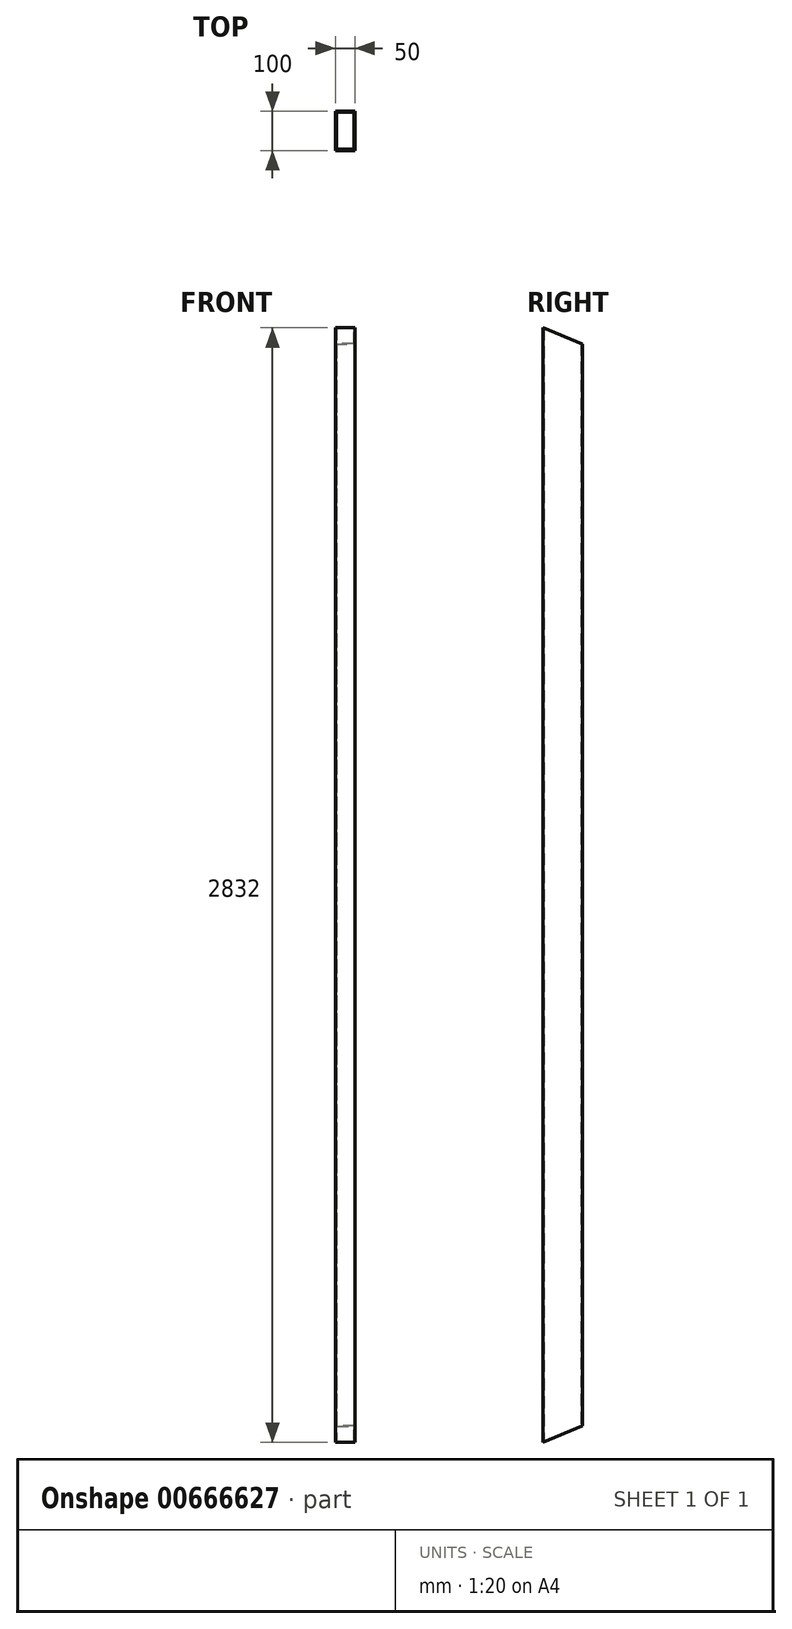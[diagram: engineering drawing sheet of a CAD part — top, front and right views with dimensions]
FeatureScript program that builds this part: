
annotation { "Feature Type Name" : "Feature", "Feature Type Description" : "" }
export const myFeature = defineFeature(function(context is Context, id is Id, definition is map)
    precondition{}
    {
        {
            var Q0;
            Q0=qCreatedBy(makeId("Top.planeOp"),FACE);
            var sketch = newSketch(context, id + "F0", { "sketchPlane" : qUnion([Q0])});
            skLineSegment(sketch, "E0.bottom", {"start": v(25, 50) * mm, "end": v(-25, 50) * mm});
            skLineSegment(sketch, "E0.top", {"start": v(25, -50) * mm, "end": v(-25, -50) * mm});
            skLineSegment(sketch, "E0.left", {"start": v(25, 50) * mm, "end": v(25, -50) * mm});
            skLineSegment(sketch, "E0.right", {"start": v(-25, 50) * mm, "end": v(-25, -50) * mm});
            skPoint(sketch, "E0.middle", {"position": v(0, 0) * mm});
            skLineSegment(sketch, "E1.bottom", {"start": v(22, 47) * mm, "end": v(-22, 47) * mm});
            skLineSegment(sketch, "E1.top", {"start": v(22, -47) * mm, "end": v(-22, -47) * mm});
            skLineSegment(sketch, "E1.left", {"start": v(22, 47) * mm, "end": v(22, -47) * mm});
            skLineSegment(sketch, "E1.right", {"start": v(-22, 47) * mm, "end": v(-22, -47) * mm});
            skSolve(sketch);
        }
        {
            var Q0;
            Q0=makeQuery(id+"F0.imprint","IMPRINT",FACE,{"disambiguationData":[TD([[makeQuery(id+"F0.imprint","IMPRINT",EDGE,{"derivedFrom":sQuery(id+"F0.wireOp",EDGE,"E0.bottom")}),1.0]])]});
            extrude(context, id + "F1", {"entities" : qUnion([Q0]), "depth" : 2832 * mm, "offsetDistance" : 25 * mm});
        }
        {
            var Q0;
            Q0=makeQuery(id+"F1.opExtrude","CAP_EDGE",EDGE,{"disambiguationData":[OSD([sQuery(id+"F0.wireOp",EDGE,"E0.bottom")])],"isStart":false});
            chamfer(context, id + "F2", {"entities" : qUnion([Q0]), "chamferType" : ChamferType.TWO_OFFSETS, "width1" : 100 * mm, "oppositeDirection" : false, "width2" : 42 * mm, "tangentPropagation" : true});
        }
        {
            var Q0;
            Q0=makeQuery(id+"F1.opExtrude","CAP_EDGE",EDGE,{"disambiguationData":[OSD([sQuery(id+"F0.wireOp",EDGE,"E0.bottom")])],"isStart":true});
            chamfer(context, id + "F3", {"entities" : qUnion([Q0]), "chamferType" : ChamferType.TWO_OFFSETS, "width1" : 42 * mm, "oppositeDirection" : false, "width2" : 100 * mm, "tangentPropagation" : true});
        }
    });
